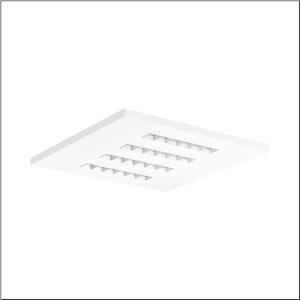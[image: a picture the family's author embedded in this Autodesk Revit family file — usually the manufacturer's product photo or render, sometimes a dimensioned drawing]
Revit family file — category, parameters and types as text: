
# Revit family: silica_r__21_square_51mx6mtst4w_73f5
name_source: partatom
category: Lighting Fixtures
units: mm (PartAtom-declared; Revit-internal decimal feet)

## family parameters
Cut with Voids When Loaded = No
Host = Face
Light Source = No
Part Type = Normal
Room Calculation Point = No
Round Connector Dimension = Use Diameter
Shared = No

## types (1)
- --- (1 x LED 2700 K ... 6500 K, 3720 lm, 30.7 W, 6500K)
    Apparent Load = 31 VA
    CIE Flux Codes = 81 98 100 100 100
    Color Rendering = 80
    Color Temperature = 6500K
    Default Elevation = 1800 mm
    Description = Silica® 21 Square, office luminaire, primary light control with lens, of PMMA, primary anti-glare with reflector, of PC, white, CAT 2 (L<= 3000cd/m²), light emission: direct distribution, primary light characteristic: symmetric, installation type: lay-in mounting, LED, rated luminous flux: 3.720lm, luminous efficacy: 113lm/W, light colour: 8tw, colour temperature: 2700..6500K, with terminal, 5-pole, mains connection: 220..240V, AC, 50/60Hz, rated input power: 32.8W, luminaire housing, of aluminium, traffic white (RAL 9016), module: M600, length: 600mm, width: 600mm, height: 32mm, protection rating (complete): IP20, insulation class (complete): insulation class I (protective earthing), certification: CE, permissible operating ambient temperature: 0..+35°C, standard: EN 50419, packaging unit: 1 piece
    Height = 0 mm  [stored 0 ft]
    Lamp = 1 x LED 2700 K ... 6500 K
    Lamp Light Flux = 3720 lm
    Lamp Power = 30.7 W
    Lamp count = 1
    Length = 597 mm
    Luminous efficacy = 121 lm/W
    Manufacturer = Siteco
    ModVariant = No
    Model = 51MX6MTST4W
    Mounting Place = Ceiling
    Mounting Type = Recessed
    Number of Poles = 1
    OnlyDefault = Yes
    Power Factor = 1
    Product Name = Silica® 21 Square
    Product group = office luminaire | ceiling recessed
    ProductGroupID = 401
    Protection Class = Protection class I
    Protection Degree = IP 20
    RLX_Detail_Level = 1
    RLX_Emergency_Light_Flux = 0 lm
    RLX_Emergency_Type = 0
    RLX_Emergency_Type_DB = No
    RlxData = <blob elided: 22401 chars, md5=fd5a1b48>
    Socket = socket
    Standby Power = 0 W
    System Light Flux = 3720 lm
    System Power = 31 W
    Type Comments = individual setting: CCT=6500K, colour temperature 6500K, luminous flux: 100 % | dim-lin: 254 | 381 mA
    Type Image = l_1275220.jpg
    URL = http://relux.com
    VarID = @adj_022561
    Voltage = 0 V
    Weight = 0.00 kg
    Width = 597 mm

note: [stored X ft] marks values corroborated as IEEE doubles in the binary element streams (Revit-internal decimal feet)

## geometry (parser evidence)
native form markers: Blend x4, Sweep x11
no freeform markers — native parametric forms only
